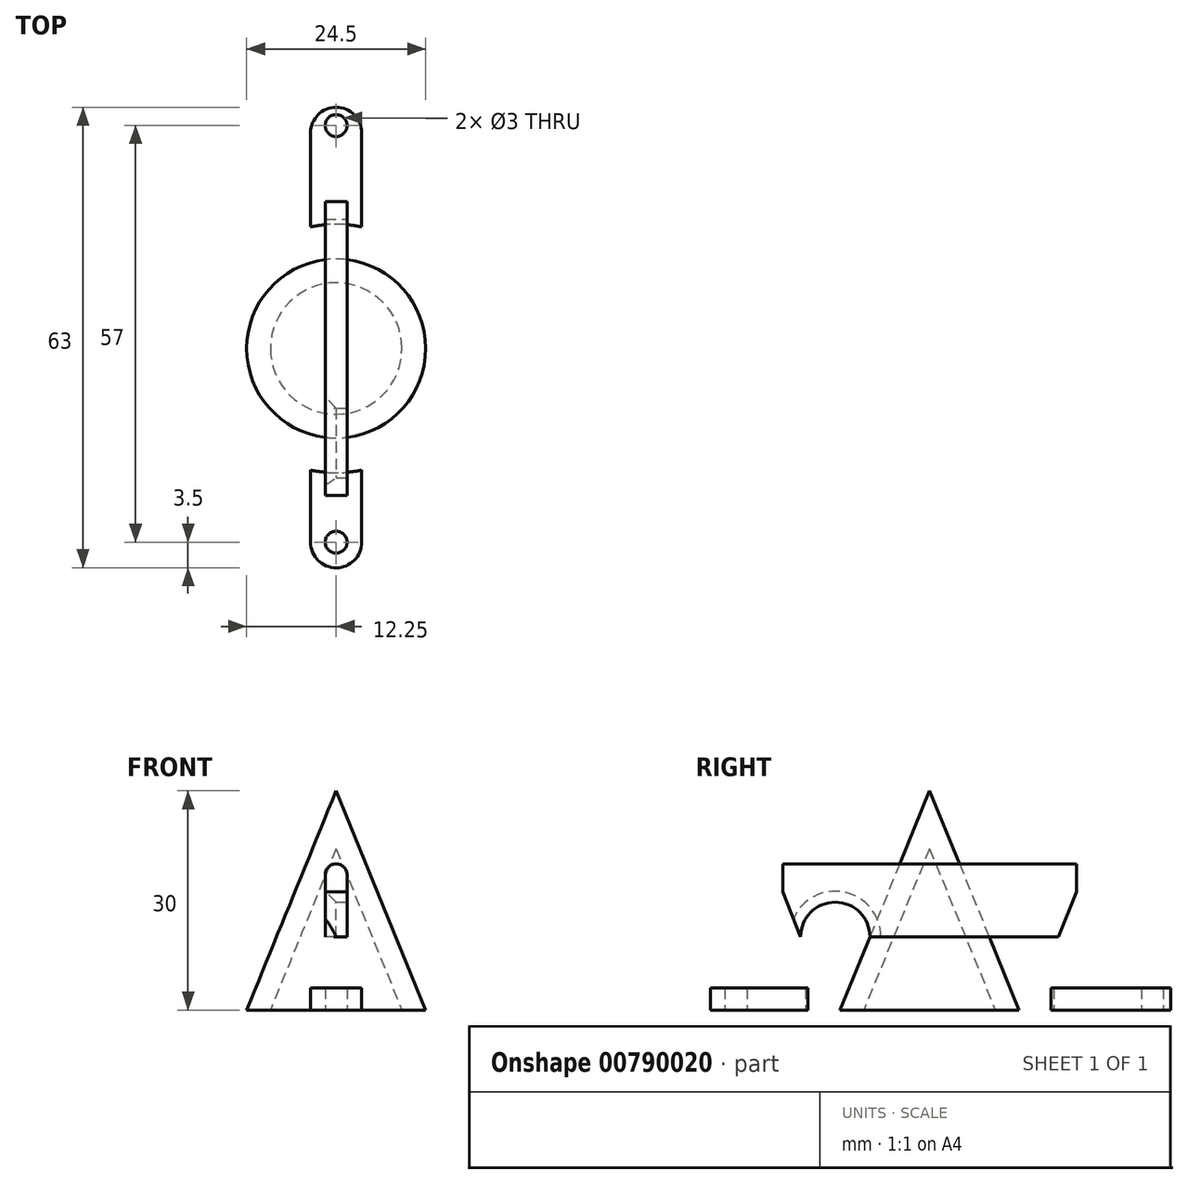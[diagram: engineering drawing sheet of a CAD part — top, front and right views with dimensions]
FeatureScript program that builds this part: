
annotation { "Feature Type Name" : "Feature", "Feature Type Description" : "" }
export const myFeature = defineFeature(function(context is Context, id is Id, definition is map)
    precondition{}
    {
        {
            var Q0;
            Q0=qCreatedBy(makeId("Top.planeOp"),FACE);
            var sketch = newSketch(context, id + "F0", { "sketchPlane" : qUnion([Q0])});
            skCircle(sketch, "E0", {"center": v(0, 0) * mm, "radius": 12.25 * mm});
            skCircle(sketch, "E1", {"center": v(0, 0) * mm, "radius": 16 * mm});
            skCircle(sketch, "E2", {"center": v(0, 0) * mm, "radius": 17 * mm});
            skLineSegment(sketch, "E3.bottom", {"start": v(-3.5, 16.52) * mm, "end": v(3.5, 16.52) * mm});
            skLineSegment(sketch, "E3.top", {"start": v(-3.5, 33) * mm, "end": v(3.5, 33) * mm});
            skLineSegment(sketch, "E3.left", {"start": v(-3.5, 16.52) * mm, "end": v(-3.5, 33) * mm});
            skLineSegment(sketch, "E3.right", {"start": v(3.5, 16.52) * mm, "end": v(3.5, 33) * mm});
            skLineSegment(sketch, "E4.bottom", {"start": v(-3.5, -16.27) * mm, "end": v(3.5, -16.27) * mm});
            skLineSegment(sketch, "E4.top", {"start": v(-3.5, -30) * mm, "end": v(3.5, -30) * mm});
            skLineSegment(sketch, "E4.left", {"start": v(-3.5, -16.27) * mm, "end": v(-3.5, -30) * mm});
            skLineSegment(sketch, "E4.right", {"start": v(3.5, -16.27) * mm, "end": v(3.5, -30) * mm});
            skPoint(sketch, "E5", {"position": v(0, -26.5) * mm});
            skPoint(sketch, "E6", {"position": v(0, 30.5) * mm});
            skSolve(sketch);
        }
        {
            var Q0;
            Q0=qCreatedBy(makeId("Front.planeOp"),FACE);
            var sketch = newSketch(context, id + "F1", { "sketchPlane" : qUnion([Q0])});
            skArc(sketch, "E7", {"start": v(-17, 0) * mm, "mid": v(-21.7, 19) * mm, "end": v(-35, 33.38) * mm});
            skArc(sketch, "E8", {"start": v(-15, 0) * mm, "mid": v(-19.93, 19.94) * mm, "end": v(-33.88, 35.03) * mm});
            skLineSegment(sketch, "E9", {"start": v(-17, 0) * mm, "end": v(-15, 0) * mm});
            skArc(sketch, "E10", {"start": v(-33.88, 35.03) * mm, "mid": v(-35.28, 34.7) * mm, "end": v(-34.91, 33.32) * mm});
            skLineSegment(sketch, "E11", {"start": v(-12.25, 0) * mm, "end": v(0, 30) * mm});
            skLineSegment(sketch, "E12", {"start": v(-12.25, 0) * mm, "end": v(-9, 0) * mm});
            skLineSegment(sketch, "E13", {"start": v(0, 0) * mm, "end": v(0, 30) * mm});
            skLineSegment(sketch, "E14", {"start": v(0, 45.67) * mm, "end": v(0, 22.06) * mm});
            skLineSegment(sketch, "E15", {"start": v(-9, 0) * mm, "end": v(0, 22.06) * mm});
            skLineSegment(sketch, "E16", {"start": v(0, 22.06) * mm, "end": v(0, 30) * mm});
            skLineSegment(sketch, "E17", {"start": v(-9, 0) * mm, "end": v(-12.25, 0) * mm});
            skLineSegment(sketch, "E18.trimOffspring", {"start": v(0, 0) * mm, "end": v(0, -5.99) * mm});
            skSolve(sketch);
        }
        {
            var Q0;
            Q0 = qSketchRegion(id + "F1", true);
            var Q1;
            Q1=sQuery(id+"F1.wireOp",EDGE,"E14");
            revolve(context, id + "F2", {"surfaceOperationType" : NewSurfaceOperationType.NEW, "entities" : qUnion([Q0]), "axis" : qUnion([Q1]), "revolveType" : RevolveType.FULL});
        }
        {
            var Q0;
            {var subQ5=sQuery(id+"F0.wireOp",EDGE,"E4.top");Q0=makeQuery(id+"F0.imprint","IMPRINT",FACE,{"disambiguationData":[TD([[makeQuery(id+"F0.imprint","IMPRINT",EDGE,{"derivedFrom":subQ5}),1.0]])]});}
            var Q1;
            {var subQ5=sQuery(id+"F0.wireOp",EDGE,"E3.top");Q1=makeQuery(id+"F0.imprint","IMPRINT",FACE,{"disambiguationData":[TD([[makeQuery(id+"F0.imprint","IMPRINT",EDGE,{"derivedFrom":subQ5}),-1.0]])]});}
            extrude(context, id + "F3", {"entities" : qUnion([Q0, Q1]), "depth" : 3 * mm, "offsetDistance" : 25 * mm});
        }
        {
            var Q0;
            Q0=sQuery(id+"F0.wireOp",VERTEX,"E6");
            var Q1;
            Q1=sQuery(id+"F0.wireOp",VERTEX,"E5");
            var Q2;
            Q2=makeQuery(id+"F3.opExtrude","SWEPT_BODY",BODY,{"disambiguationData":[OSD([sQuery(id+"F0.wireOp",EDGE,"E2"),sQuery(id+"F0.wireOp",EDGE,"EUItidCD-o9oz-pEAf-MDVd-OqGDECdkKYsf.top"),sQuery(id+"F0.wireOp",EDGE,"EUItidCD-o9oz-pEAf-MDVd-OqGDECdkKYsf.left"),sQuery(id+"F0.wireOp",EDGE,"EUItidCD-o9oz-pEAf-MDVd-OqGDECdkKYsf.right")])]});
            var Q3;
            Q3=makeQuery(id+"F3.opExtrude","SWEPT_BODY",BODY,{"disambiguationData":[OSD([sQuery(id+"F0.wireOp",EDGE,"E2"),sQuery(id+"F0.wireOp",EDGE,"TQropyhq-qoue-lAR9-v35R-7amXnqsSdPZm.top"),sQuery(id+"F0.wireOp",EDGE,"TQropyhq-qoue-lAR9-v35R-7amXnqsSdPZm.left"),sQuery(id+"F0.wireOp",EDGE,"TQropyhq-qoue-lAR9-v35R-7amXnqsSdPZm.right")])]});
            hole(context, id + "F4", {"style" : HoleStyle.SIMPLE, "endStyle" : HoleEndStyle.BLIND, "oppositeDirection" : true, "holeDiameter" : 3 * mm, "majorDiameter" : 5 * mm, "holeDepth" : 15.8 * mm, "isTappedThrough" : true, "tappedDepth" : 12 * mm, "tapClearance" : 3, "startFromSketch" : true, "locations" : qUnion([Q0, Q1]), "scope" : qUnion([Q2, Q3])});
        }
        {
            var Q0;
            Q0=qCreatedBy(makeId("Front.planeOp"),FACE);
            var sketch = newSketch(context, id + "F5", { "sketchPlane" : qUnion([Q0])});
            skLineSegment(sketch, "E19.bottom", {"start": v(-1.5, 20) * mm, "end": v(1.5, 20) * mm});
            skLineSegment(sketch, "E19.top", {"start": v(-1.5, 10) * mm, "end": v(1.5, 10) * mm});
            skLineSegment(sketch, "E19.left", {"start": v(-1.5, 20) * mm, "end": v(-1.5, 10) * mm});
            skLineSegment(sketch, "E19.right", {"start": v(1.5, 20) * mm, "end": v(1.5, 10) * mm});
            skSolve(sketch);
        }
        {
            var Q0;
            Q0 = qSketchRegion(id + "F5", true);
            extrude(context, id + "F6", {"entities" : qUnion([Q0]), "endBound" : BoundingType.SYMMETRIC, "depth" : 40.2 * mm, "offsetDistance" : 25 * mm});
        }
        {
            var Q0;
            Q0=makeQuery(id+"F6.opExtrude","SWEPT_EDGE",EDGE,{"disambiguationData":[OSD([sQuery(id+"F5.wireOp",EDGE,"E19.bottom"),sQuery(id+"F5.wireOp",EDGE,"E19.right")])]});
            var Q1;
            Q1=makeQuery(id+"F6.opExtrude","SWEPT_EDGE",EDGE,{"disambiguationData":[OSD([sQuery(id+"F5.wireOp",EDGE,"E19.bottom"),sQuery(id+"F5.wireOp",EDGE,"E19.left")])]});
            fillet(context, id + "F7", {"entities" : qUnion([Q0, Q1]), "radius" : 1.5 * mm, "tangentPropagation" : true, "allowEdgeOverflow" : false});
        }
        {
            var Q0;
            Q0=makeQuery(id+"F6.opExtrude","SWEPT_FACE",FACE,{"disambiguationData":[OSD([sQuery(id+"F5.wireOp",EDGE,"E19.right")])]});
            var sketch = newSketch(context, id + "F8", { "sketchPlane" : qUnion([Q0])});
            skCircle(sketch, "E20", {"center": v(-12.91, 10) * mm, "radius": 4.75 * mm});
            skLineSegment(sketch, "E21", {"start": v(-20.46, 17.1) * mm, "end": v(-17.66, 10) * mm});
            skLineSegment(sketch, "E22", {"start": v(-17.66, 10) * mm, "end": v(-20.93, 8.38) * mm});
            skLineSegment(sketch, "E23", {"start": v(-20.93, 8.38) * mm, "end": v(-20.46, 17.1) * mm});
            skLineSegment(sketch, "E24", {"start": v(0, 43.45) * mm, "end": v(0, -6.53) * mm});
            skLineSegment(sketch, "E25.MirrorCS", {"start": v(20.93, 8.38) * mm, "end": v(20.46, 17.1) * mm});
            skLineSegment(sketch, "E26.MirrorCS", {"start": v(17.66, 10) * mm, "end": v(20.93, 8.38) * mm});
            skLineSegment(sketch, "E27.MirrorCS", {"start": v(20.46, 17.1) * mm, "end": v(17.66, 10) * mm});
            skCircle(sketch, "E28.MirrorC", {"center": v(12.91, 10) * mm, "radius": 4.75 * mm});
            skSolve(sketch);
        }
        {
            var Q0;
            {var subQ0=sQuery(id+"F8.wireOp",EDGE,"E20");var subQ1=makeQuery(id+"F6.opExtrude","SWEPT_EDGE",EDGE,{"disambiguationData":[OSD([sQuery(id+"F5.wireOp",EDGE,"E19.top"),sQuery(id+"F5.wireOp",EDGE,"E19.right")])]});var subQ3=makeQuery(id+"F8.imprint","INTERSECT",VERTEX,{"derivedFrom":[subQ1,subQ0]});Q0=makeQuery(id+"F8.imprint","IMPRINT",FACE,{"disambiguationData":[TD([[makeQuery(id+"F8.imprint","IMPRINT",EDGE,{"disambiguationData":[TD([[subQ3,-1.0]])],"derivedFrom":subQ0}),1.0]])]});}
            var Q1;
            {var subQ0=sQuery(id+"F8.wireOp",EDGE,"E28.MirrorC");var subQ1=makeQuery(id+"F6.opExtrude","SWEPT_EDGE",EDGE,{"disambiguationData":[OSD([sQuery(id+"F5.wireOp",EDGE,"E19.top"),sQuery(id+"F5.wireOp",EDGE,"E19.right")])]});var subQ3=makeQuery(id+"F8.imprint","INTERSECT",VERTEX,{"derivedFrom":[subQ1,subQ0]});Q1=makeQuery(id+"F8.imprint","IMPRINT",FACE,{"disambiguationData":[TD([[makeQuery(id+"F8.imprint","IMPRINT",EDGE,{"disambiguationData":[TD([[subQ3,-1.0]])],"derivedFrom":subQ0}),-1.0]])]});}
            var Q2;
            {var subQ0=sQuery(id+"F8.wireOp",EDGE,"E21");var subQ1=sQuery(id+"F5.wireOp",EDGE,"E19.right");var subQ4=makeQuery(id+"F6.opExtrude","CAP_EDGE",EDGE,{"disambiguationData":[OSD([subQ1])],"isStart":false});var subQ5=makeQuery(id+"F8.imprint","INTERSECT",VERTEX,{"derivedFrom":[subQ4,subQ0]});Q2=makeQuery(id+"F8.imprint","IMPRINT",FACE,{"disambiguationData":[TD([[makeQuery(id+"F8.imprint","IMPRINT",EDGE,{"disambiguationData":[TD([[subQ5,-1.0]])],"derivedFrom":subQ4}),1.0]])]});}
            var Q3;
            {var subQ0=sQuery(id+"F8.wireOp",EDGE,"E27.MirrorCS");var subQ1=sQuery(id+"F5.wireOp",EDGE,"E19.right");var subQ4=makeQuery(id+"F6.opExtrude","CAP_EDGE",EDGE,{"disambiguationData":[OSD([subQ1])],"isStart":true});var subQ5=makeQuery(id+"F8.imprint","INTERSECT",VERTEX,{"derivedFrom":[subQ4,subQ0]});Q3=makeQuery(id+"F8.imprint","IMPRINT",FACE,{"disambiguationData":[TD([[makeQuery(id+"F8.imprint","IMPRINT",EDGE,{"disambiguationData":[TD([[subQ5,-1.0]])],"derivedFrom":subQ4}),-1.0]])]});}
            extrude(context, id + "F9", {"entities" : qUnion([Q0, Q1, Q2, Q3]), "operationType" : NewBodyOperationType.REMOVE, "oppositeDirection" : true, "depth" : 25 * mm, "offsetDistance" : 25 * mm});
        }
        {
            var Q0;
            Q0=makeQuery(id+"F9.boolean.opBoolean","COPY",EDGE,{"derivedFrom":makeQuery(id+"F9.opExtrude","CAP_EDGE",EDGE,{"disambiguationData":[OSD([sQuery(id+"F8.wireOp",EDGE,"E20")])],"isStart":true})});
            var Q1;
            Q1=makeQuery(id+"F9.boolean.opBoolean","COPY",EDGE,{"derivedFrom":makeQuery(id+"F9.opExtrude","CAP_EDGE",EDGE,{"disambiguationData":[OSD([sQuery(id+"F8.wireOp",EDGE,"E28.MirrorC")])],"isStart":true})});
            var Q2;
            Q2=makeQuery(id+"F9.boolean.opBoolean","INTERSECT",EDGE,{"derivedFrom":[makeQuery(id+"F6.opExtrude","SWEPT_FACE",FACE,{"disambiguationData":[OSD([sQuery(id+"F5.wireOp",EDGE,"E19.left")])]}),makeQuery(id+"F9.opExtrude","SWEPT_FACE",FACE,{"disambiguationData":[OSD([sQuery(id+"F8.wireOp",EDGE,"E28.MirrorC")])]})]});
            var Q3;
            Q3=makeQuery(id+"F9.boolean.opBoolean","INTERSECT",EDGE,{"derivedFrom":[makeQuery(id+"F6.opExtrude","SWEPT_FACE",FACE,{"disambiguationData":[OSD([sQuery(id+"F5.wireOp",EDGE,"E19.left")])]}),makeQuery(id+"F9.opExtrude","SWEPT_FACE",FACE,{"disambiguationData":[OSD([sQuery(id+"F8.wireOp",EDGE,"E20")])]})]});
            chamfer(context, id + "F10", {"entities" : qUnion([Q0, Q1, Q2, Q3]), "width" : 1.5 * mm, "tangentPropagation" : true});
        }
        {
            var Q0;
            Q0=makeQuery(id+"F3.opExtrude","SWEPT_EDGE",EDGE,{"disambiguationData":[OSD([sQuery(id+"F0.wireOp",EDGE,"E3.top"),sQuery(id+"F0.wireOp",EDGE,"E3.left")])]});
            var Q1;
            Q1=makeQuery(id+"F3.opExtrude","SWEPT_EDGE",EDGE,{"disambiguationData":[OSD([sQuery(id+"F0.wireOp",EDGE,"E3.top"),sQuery(id+"F0.wireOp",EDGE,"E3.right")])]});
            var Q2;
            Q2=makeQuery(id+"F3.opExtrude","SWEPT_EDGE",EDGE,{"disambiguationData":[OSD([sQuery(id+"F0.wireOp",EDGE,"E4.top"),sQuery(id+"F0.wireOp",EDGE,"E4.left")])]});
            var Q3;
            Q3=makeQuery(id+"F3.opExtrude","SWEPT_EDGE",EDGE,{"disambiguationData":[OSD([sQuery(id+"F0.wireOp",EDGE,"E4.top"),sQuery(id+"F0.wireOp",EDGE,"E4.right")])]});
            fillet(context, id + "F11", {"entities" : qUnion([Q0, Q1, Q2, Q3]), "radius" : 3.5 * mm, "tangentPropagation" : true, "allowEdgeOverflow" : false});
        }
    });
